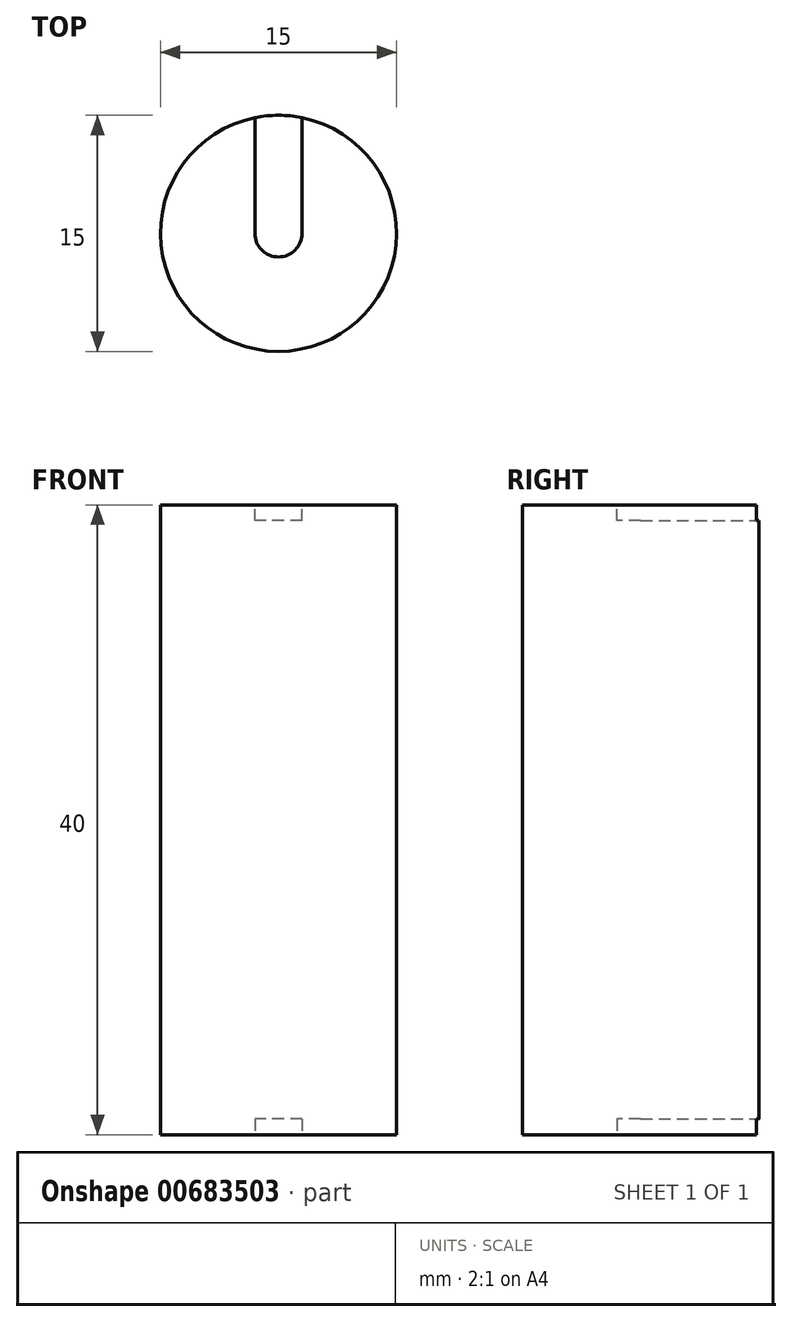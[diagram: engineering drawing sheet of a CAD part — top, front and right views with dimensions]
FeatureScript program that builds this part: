
annotation { "Feature Type Name" : "Feature", "Feature Type Description" : "" }
export const myFeature = defineFeature(function(context is Context, id is Id, definition is map)
    precondition{}
    {
        {
            var Q0;
            Q0=qCreatedBy(makeId("Top.planeOp"),FACE);
            var sketch = newSketch(context, id + "F0", { "sketchPlane" : qUnion([Q0])});
            skCircle(sketch, "E0", {"center": v(0, 0) * mm, "radius": 7.5 * mm});
            skArc(sketch, "E1", {"start": v(-1.5, 0) * mm, "mid": v(0, -1.5) * mm, "end": v(1.5, 0) * mm});
            skLineSegment(sketch, "E2", {"start": v(-1.5, 0) * mm, "end": v(-1.5, 7.35) * mm});
            skLineSegment(sketch, "E3", {"start": v(1.5, 0) * mm, "end": v(1.5, 7.35) * mm});
            skSolve(sketch);
        }
        {
            var Q0;
            Q0 = qSketchRegion(id + "F0", true);
            extrude(context, id + "F1", {"entities" : qUnion([Q0]), "depth" : 40 * mm, "offsetDistance" : 25 * mm});
        }
        {
            var Q0;
            Q0=makeQuery(id+"F0.imprint","IMPRINT",FACE,{"disambiguationData":[TD([[makeQuery(id+"F0.imprint","IMPRINT",EDGE,{"derivedFrom":sQuery(id+"F0.wireOp",EDGE,"E1")}),1.0]])]});
            extrude(context, id + "F2", {"entities" : qUnion([Q0]), "operationType" : NewBodyOperationType.REMOVE, "depth" : 1 * mm, "offsetDistance" : 25 * mm});
        }
        {
            var Q0;
            Q0=makeQuery(id+"F1.opExtrude","CAP_FACE",FACE,{"disambiguationData":[OSD([sQuery(id+"F0.wireOp",EDGE,"E0")])],"isStart":false});
            var sketch = newSketch(context, id + "F3", { "sketchPlane" : qUnion([Q0])});
            skLineSegment(sketch, "E4.0", {"start": v(1.5, 0) * mm, "end": v(1.5, 7.35) * mm});
            skArc(sketch, "E5.0", {"start": v(-1.5, 0) * mm, "mid": v(0, -1.5) * mm, "end": v(1.5, 0) * mm});
            skLineSegment(sketch, "E6.0", {"start": v(-1.5, 0) * mm, "end": v(-1.5, 7.35) * mm});
            skCircle(sketch, "E7.0", {"center": v(0, 0) * mm, "radius": 7.5 * mm});
            skSolve(sketch);
        }
        {
            var Q0;
            {var subQ0=sQuery(id+"F3.wireOp",EDGE,"E4.0");Q0=makeQuery(id+"F3.imprint","IMPRINT",FACE,{"disambiguationData":[TD([[makeQuery(id+"F3.imprint","IMPRINT",EDGE,{"derivedFrom":subQ0}),1.0]])]});}
            extrude(context, id + "F4", {"entities" : qUnion([Q0]), "operationType" : NewBodyOperationType.REMOVE, "oppositeDirection" : true, "depth" : 1 * mm, "offsetDistance" : 25 * mm});
        }
    });
